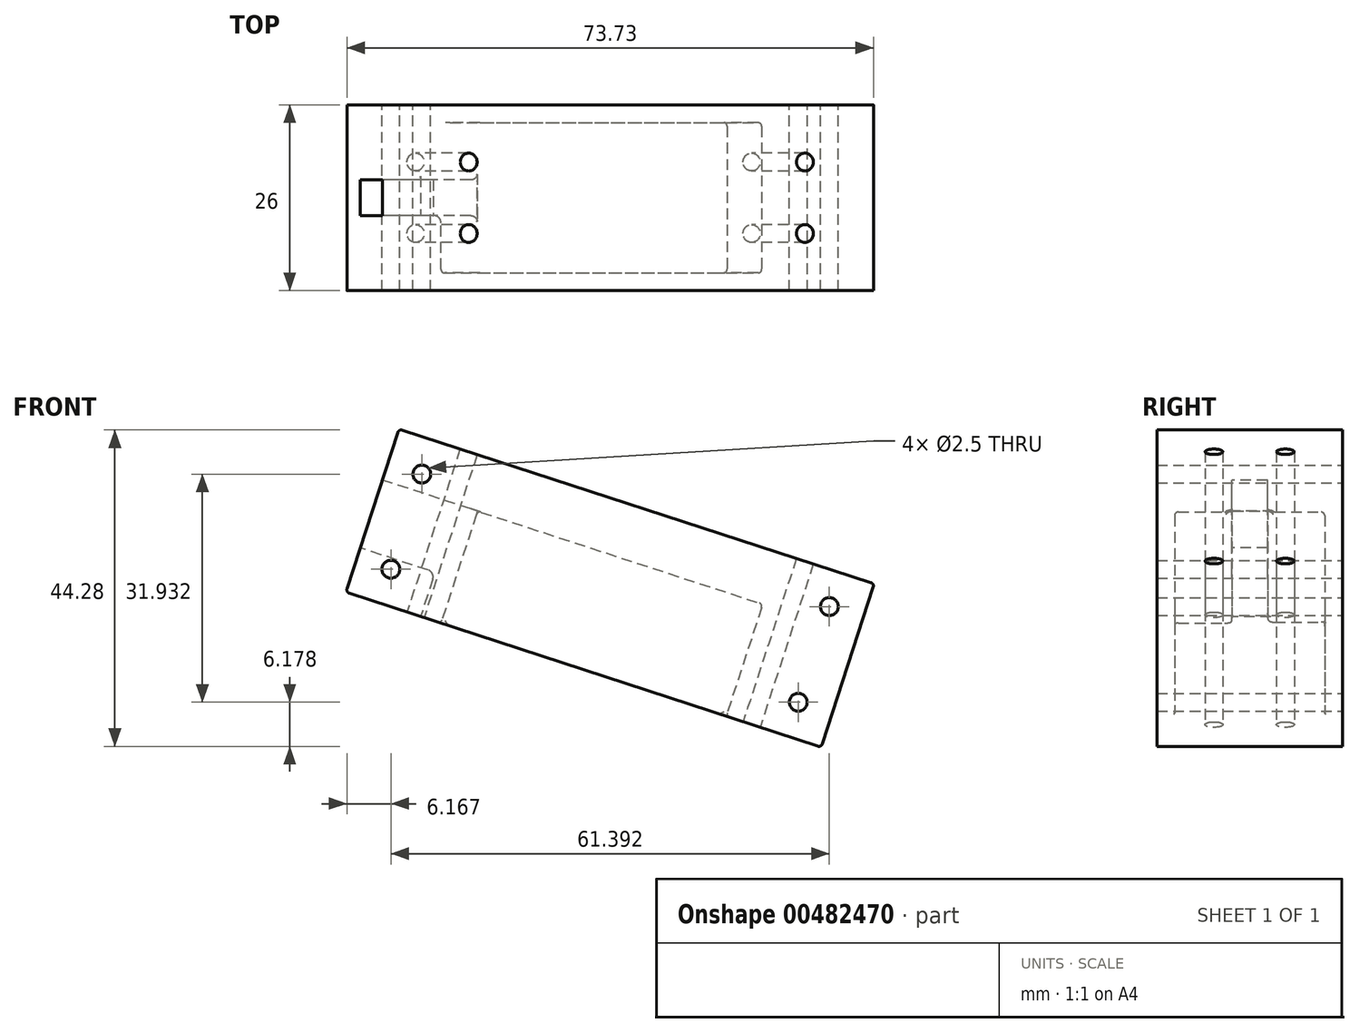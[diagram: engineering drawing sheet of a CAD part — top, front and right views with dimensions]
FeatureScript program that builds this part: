
annotation { "Feature Type Name" : "Feature", "Feature Type Description" : "" }
export const myFeature = defineFeature(function(context is Context, id is Id, definition is map)
    precondition{}
    {
        {
            var Q0;
            Q0=qCreatedBy(makeId("Front.planeOp"),FACE);
            var sketch = newSketch(context, id + "F0", { "sketchPlane" : qUnion([Q0])});
            skLineSegment(sketch, "E0", {"start": v(-70.96, 25.55) * mm, "end": v(-63.54, 48.37) * mm});
            skPoint(sketch, "E1", {"position": v(-64.66, 28.75) * mm});
            skPoint(sketch, "E2", {"position": v(-60.33, 42.07) * mm});
            skLineSegment(sketch, "E3", {"start": v(3.03, 26.74) * mm, "end": v(-4.41, 3.83) * mm});
            skPoint(sketch, "E4", {"position": v(-3.27, 23.53) * mm});
            skPoint(sketch, "E5", {"position": v(-7.62, 10.14) * mm});
            skCircle(sketch, "E6", {"center": v(-60.33, 42.07) * mm, "radius": 1.25 * mm});
            skCircle(sketch, "E7", {"center": v(-64.66, 28.75) * mm, "radius": 1.25 * mm});
            skCircle(sketch, "E8", {"center": v(-3.27, 23.53) * mm, "radius": 1.25 * mm});
            skCircle(sketch, "E9", {"center": v(-7.62, 10.14) * mm, "radius": 1.25 * mm});
            skLineSegment(sketch, "E10", {"start": v(-70.96, 25.55) * mm, "end": v(-4.41, 3.83) * mm});
            skLineSegment(sketch, "E11", {"start": v(-63.54, 48.37) * mm, "end": v(3.03, 26.74) * mm});
            skSolve(sketch);
        }
        {
            var Q0;
            Q0 = qSketchRegion(id + "F0", true);
            extrude(context, id + "F1", {"entities" : qUnion([Q0]), "depth" : 26 * mm, "offsetDistance" : 25 * mm});
        }
        {
            var Q0;
            Q0=makeQuery(id+"F1.opExtrude","SWEPT_FACE",FACE,{"disambiguationData":[OSD([sQuery(id+"F0.wireOp",EDGE,"E10")])]});
            var sketch = newSketch(context, id + "F2", { "sketchPlane" : qUnion([Q0])});
            skCircle(sketch, "E12", {"center": v(-65.13, 18) * mm, "radius": 1.25 * mm});
            skCircle(sketch, "E13", {"center": v(-65.13, 8) * mm, "radius": 1.25 * mm});
            skCircle(sketch, "E14", {"center": v(-15.63, 18) * mm, "radius": 1.25 * mm});
            skCircle(sketch, "E15", {"center": v(-15.63, 8) * mm, "radius": 1.25 * mm});
            skLineSegment(sketch, "E16.bottom", {"start": v(-61.38, 23.5) * mm, "end": v(-19.38, 23.5) * mm});
            skLineSegment(sketch, "E16.top", {"start": v(-61.38, 2.5) * mm, "end": v(-19.38, 2.5) * mm});
            skLineSegment(sketch, "E16.left", {"start": v(-61.38, 23.5) * mm, "end": v(-61.38, 15.5) * mm});
            skLineSegment(sketch, "E16.right", {"start": v(-19.38, 23.5) * mm, "end": v(-19.38, 2.5) * mm});
            skLineSegment(sketch, "E17.bottom", {"start": v(-61.38, 10.5) * mm, "end": v(-64.38, 10.5) * mm});
            skLineSegment(sketch, "E17.top", {"start": v(-61.38, 15.5) * mm, "end": v(-64.38, 15.5) * mm});
            skLineSegment(sketch, "E17.right", {"start": v(-64.38, 10.5) * mm, "end": v(-64.38, 15.5) * mm});
            skLineSegment(sketch, "E18.trimOffspring", {"start": v(-61.38, 10.5) * mm, "end": v(-61.38, 2.5) * mm});
            skSolve(sketch);
        }
        {
            var Q0;
            Q0=makeQuery(id+"F2.imprint","IMPRINT",FACE,{"disambiguationData":[TD([[makeQuery(id+"F2.imprint","IMPRINT",EDGE,{"derivedFrom":sQuery(id+"F2.wireOp",EDGE,"E12")}),1.0]])]});
            var Q1;
            Q1=makeQuery(id+"F2.imprint","IMPRINT",FACE,{"disambiguationData":[TD([[makeQuery(id+"F2.imprint","IMPRINT",EDGE,{"derivedFrom":sQuery(id+"F2.wireOp",EDGE,"E13")}),1.0]])]});
            var Q2;
            Q2=makeQuery(id+"F2.imprint","IMPRINT",FACE,{"disambiguationData":[TD([[makeQuery(id+"F2.imprint","IMPRINT",EDGE,{"derivedFrom":sQuery(id+"F2.wireOp",EDGE,"E14")}),1.0]])]});
            var Q3;
            Q3=makeQuery(id+"F2.imprint","IMPRINT",FACE,{"disambiguationData":[TD([[makeQuery(id+"F2.imprint","IMPRINT",EDGE,{"derivedFrom":sQuery(id+"F2.wireOp",EDGE,"E15")}),1.0]])]});
            extrude(context, id + "F3", {"entities" : qUnion([Q0, Q1, Q2, Q3]), "operationType" : NewBodyOperationType.REMOVE, "oppositeDirection" : true, "depth" : 25 * mm, "offsetDistance" : 25 * mm});
        }
        {
            var Q0;
            Q0=makeQuery(id+"F2.imprint","IMPRINT",FACE,{"disambiguationData":[TD([[makeQuery(id+"F2.imprint","IMPRINT",EDGE,{"derivedFrom":sQuery(id+"F2.wireOp",EDGE,"E16.bottom")}),-1.0]])]});
            extrude(context, id + "F4", {"entities" : qUnion([Q0]), "operationType" : NewBodyOperationType.REMOVE, "oppositeDirection" : true, "depth" : 16.5 * mm, "offsetDistance" : 25 * mm});
        }
        {
            var Q0;
            Q0=makeQuery(id+"F1.opExtrude","SWEPT_FACE",FACE,{"disambiguationData":[OSD([sQuery(id+"F0.wireOp",EDGE,"E0")])]});
            var sketch = newSketch(context, id + "F5", { "sketchPlane" : qUnion([Q0])});
            skLineSegment(sketch, "E19", {"start": v(13, 0) * mm, "end": v(13, 27.29) * mm, "construction": true});
            skLineSegment(sketch, "E20.bottom", {"start": v(10.5, 8.87) * mm, "end": v(15.5, 8.87) * mm});
            skLineSegment(sketch, "E20.top", {"start": v(10.5, 18.87) * mm, "end": v(15.5, 18.87) * mm});
            skLineSegment(sketch, "E20.left", {"start": v(10.5, 8.87) * mm, "end": v(10.5, 18.87) * mm});
            skLineSegment(sketch, "E20.right", {"start": v(15.5, 8.87) * mm, "end": v(15.5, 18.87) * mm});
            skSolve(sketch);
        }
        {
            var Q0;
            Q0=makeQuery(id+"F5.imprint","IMPRINT",FACE,{"disambiguationData":[TD([[makeQuery(id+"F5.imprint","IMPRINT",EDGE,{"derivedFrom":sQuery(id+"F5.wireOp",EDGE,"E20.bottom")}),1.0]])]});
            extrude(context, id + "F6", {"entities" : qUnion([Q0]), "operationType" : NewBodyOperationType.REMOVE, "oppositeDirection" : true, "depth" : 14 * mm, "offsetDistance" : 25 * mm});
        }
        {
            var Q0;
            Q0=makeQuery(id+"F6.boolean.opBoolean","COPY",EDGE,{"derivedFrom":makeQuery(id+"F6.opExtrude","CAP_EDGE",EDGE,{"disambiguationData":[OSD([sQuery(id+"F5.wireOp",EDGE,"E20.left")])],"isStart":true})});
            var Q1;
            Q1=makeQuery(id+"F6.boolean.opBoolean","COPY",EDGE,{"derivedFrom":makeQuery(id+"F6.opExtrude","CAP_EDGE",EDGE,{"disambiguationData":[OSD([sQuery(id+"F5.wireOp",EDGE,"E20.right")])],"isStart":true})});
            var Q2;
            Q2=makeQuery(id+"F6.boolean.opBoolean","COPY",EDGE,{"derivedFrom":makeQuery(id+"F6.opExtrude","CAP_EDGE",EDGE,{"disambiguationData":[OSD([sQuery(id+"F5.wireOp",EDGE,"E20.top")])],"isStart":true})});
            var Q3;
            Q3=makeQuery(id+"F6.boolean.opBoolean","COPY",EDGE,{"derivedFrom":makeQuery(id+"F6.opExtrude","CAP_EDGE",EDGE,{"disambiguationData":[OSD([sQuery(id+"F5.wireOp",EDGE,"E20.bottom")])],"isStart":true})});
            var Q4;
            Q4=makeQuery(id+"F4.boolean.opBoolean","COPY",EDGE,{"derivedFrom":makeQuery(id+"F4.opExtrude","SWEPT_EDGE",EDGE,{"disambiguationData":[OSD([sQuery(id+"F2.wireOp",EDGE,"E16.left"),sQuery(id+"F2.wireOp",EDGE,"E17.top")])]})});
            var Q5;
            Q5=makeQuery(id+"F4.boolean.opBoolean","COPY",EDGE,{"derivedFrom":makeQuery(id+"F4.opExtrude","SWEPT_EDGE",EDGE,{"disambiguationData":[OSD([sQuery(id+"F2.wireOp",EDGE,"E17.bottom"),sQuery(id+"F2.wireOp",EDGE,"E18.trimOffspring")])]})});
            var Q6;
            Q6=makeQuery(id+"F6.boolean.opBoolean","INTERSECT",EDGE,{"derivedFrom":[makeQuery(id+"F4.boolean.opBoolean","COPY",FACE,{"derivedFrom":makeQuery(id+"F4.opExtrude","SWEPT_FACE",FACE,{"disambiguationData":[OSD([sQuery(id+"F2.wireOp",EDGE,"E17.right")])]})}),makeQuery(id+"F6.opExtrude","SWEPT_FACE",FACE,{"disambiguationData":[OSD([sQuery(id+"F5.wireOp",EDGE,"E20.bottom")])]})]});
            fillet(context, id + "F7", {"entities" : qUnion([Q0, Q1, Q2, Q3, Q4, Q5, Q6]), "radius" : 1 * mm, "tangentPropagation" : true, "allowEdgeOverflow" : false});
        }
        {
            var Q0;
            Q0=makeQuery(id+"F4.boolean.opBoolean","COPY",EDGE,{"derivedFrom":makeQuery(id+"F4.opExtrude","CAP_EDGE",EDGE,{"disambiguationData":[OSD([sQuery(id+"F2.wireOp",EDGE,"E16.left")])],"isStart":true})});
            var Q1;
            Q1=makeQuery(id+"F4.boolean.opBoolean","COPY",EDGE,{"derivedFrom":makeQuery(id+"F4.opExtrude","CAP_EDGE",EDGE,{"disambiguationData":[OSD([sQuery(id+"F2.wireOp",EDGE,"E17.right")])],"isStart":true})});
            var Q2;
            Q2=makeQuery(id+"F4.boolean.opBoolean","COPY",EDGE,{"derivedFrom":makeQuery(id+"F4.opExtrude","CAP_EDGE",EDGE,{"disambiguationData":[OSD([sQuery(id+"F2.wireOp",EDGE,"E17.bottom")])],"isStart":true})});
            var Q3;
            Q3=makeQuery(id+"F7.opFillet","BLEND_EDGE",EDGE,{"blendedFrom":[makeQuery(id+"F4.boolean.opBoolean","COPY",EDGE,{"derivedFrom":makeQuery(id+"F4.opExtrude","SWEPT_EDGE",EDGE,{"disambiguationData":[OSD([sQuery(id+"F2.wireOp",EDGE,"E17.bottom"),sQuery(id+"F2.wireOp",EDGE,"E18.trimOffspring")])]})}),makeQuery(id+"F1.opExtrude","SWEPT_FACE",FACE,{"disambiguationData":[OSD([sQuery(id+"F0.wireOp",EDGE,"E10")])]})],"blendedInto":[makeQuery(id+"F1.opExtrude","SWEPT_FACE",FACE,{"disambiguationData":[OSD([sQuery(id+"F0.wireOp",EDGE,"E10")])]})]});
            var Q4;
            Q4=makeQuery(id+"F4.boolean.opBoolean","COPY",EDGE,{"derivedFrom":makeQuery(id+"F4.opExtrude","CAP_EDGE",EDGE,{"disambiguationData":[OSD([sQuery(id+"F2.wireOp",EDGE,"E16.bottom")])],"isStart":true})});
            var Q5;
            Q5=makeQuery(id+"F4.boolean.opBoolean","COPY",EDGE,{"derivedFrom":makeQuery(id+"F4.opExtrude","SWEPT_EDGE",EDGE,{"disambiguationData":[OSD([sQuery(id+"F2.wireOp",EDGE,"E16.bottom"),sQuery(id+"F2.wireOp",EDGE,"E16.left")])]})});
            var Q6;
            Q6=makeQuery(id+"F4.boolean.opBoolean","COPY",EDGE,{"derivedFrom":makeQuery(id+"F4.opExtrude","CAP_EDGE",EDGE,{"disambiguationData":[OSD([sQuery(id+"F2.wireOp",EDGE,"E16.left")])],"isStart":false})});
            var Q7;
            Q7=makeQuery(id+"F4.boolean.opBoolean","COPY",EDGE,{"derivedFrom":makeQuery(id+"F4.opExtrude","CAP_EDGE",EDGE,{"disambiguationData":[OSD([sQuery(id+"F2.wireOp",EDGE,"E16.bottom")])],"isStart":false})});
            var Q8;
            Q8=makeQuery(id+"F4.boolean.opBoolean","COPY",EDGE,{"derivedFrom":makeQuery(id+"F4.opExtrude","CAP_EDGE",EDGE,{"disambiguationData":[OSD([sQuery(id+"F2.wireOp",EDGE,"E18.trimOffspring")])],"isStart":false})});
            var Q9;
            Q9=makeQuery(id+"F4.boolean.opBoolean","COPY",EDGE,{"derivedFrom":makeQuery(id+"F4.opExtrude","SWEPT_EDGE",EDGE,{"disambiguationData":[OSD([sQuery(id+"F2.wireOp",EDGE,"E16.top"),sQuery(id+"F2.wireOp",EDGE,"E18.trimOffspring")])]})});
            var Q10;
            Q10=makeQuery(id+"F4.boolean.opBoolean","COPY",EDGE,{"derivedFrom":makeQuery(id+"F4.opExtrude","CAP_EDGE",EDGE,{"disambiguationData":[OSD([sQuery(id+"F2.wireOp",EDGE,"E16.top")])],"isStart":false})});
            var Q11;
            Q11=makeQuery(id+"F4.boolean.opBoolean","COPY",EDGE,{"derivedFrom":makeQuery(id+"F4.opExtrude","CAP_EDGE",EDGE,{"disambiguationData":[OSD([sQuery(id+"F2.wireOp",EDGE,"E16.top")])],"isStart":true})});
            var Q12;
            Q12=makeQuery(id+"F4.boolean.opBoolean","COPY",FACE,{"derivedFrom":makeQuery(id+"F4.opExtrude","SWEPT_FACE",FACE,{"disambiguationData":[OSD([sQuery(id+"F2.wireOp",EDGE,"E16.right")])]})});
            var Q13;
            Q13=makeQuery(id+"F4.boolean.opBoolean","COPY",EDGE,{"derivedFrom":makeQuery(id+"F4.opExtrude","CAP_EDGE",EDGE,{"disambiguationData":[OSD([sQuery(id+"F2.wireOp",EDGE,"E18.trimOffspring")])],"isStart":true})});
            var Q14;
            Q14=makeQuery(id+"F1.opExtrude","SWEPT_EDGE",EDGE,{"disambiguationData":[OSD([sQuery(id+"F0.wireOp",EDGE,"E0"),sQuery(id+"F0.wireOp",EDGE,"E10")])]});
            var Q15;
            Q15=makeQuery(id+"F1.opExtrude","SWEPT_EDGE",EDGE,{"disambiguationData":[OSD([sQuery(id+"F0.wireOp",EDGE,"E3"),sQuery(id+"F0.wireOp",EDGE,"E10")])]});
            var Q16;
            Q16=makeQuery(id+"F1.opExtrude","SWEPT_EDGE",EDGE,{"disambiguationData":[OSD([sQuery(id+"F0.wireOp",EDGE,"E3"),sQuery(id+"F0.wireOp",EDGE,"E11")])]});
            var Q17;
            Q17=makeQuery(id+"F1.opExtrude","SWEPT_EDGE",EDGE,{"disambiguationData":[OSD([sQuery(id+"F0.wireOp",EDGE,"E0"),sQuery(id+"F0.wireOp",EDGE,"E11")])]});
            fillet(context, id + "F8", {"entities" : qUnion([Q0, Q1, Q2, Q3, Q4, Q5, Q6, Q7, Q8, Q9, Q10, Q11, Q12, Q13, Q14, Q15, Q16, Q17]), "radius" : .5 * mm, "tangentPropagation" : true, "allowEdgeOverflow" : false});
        }
    });
